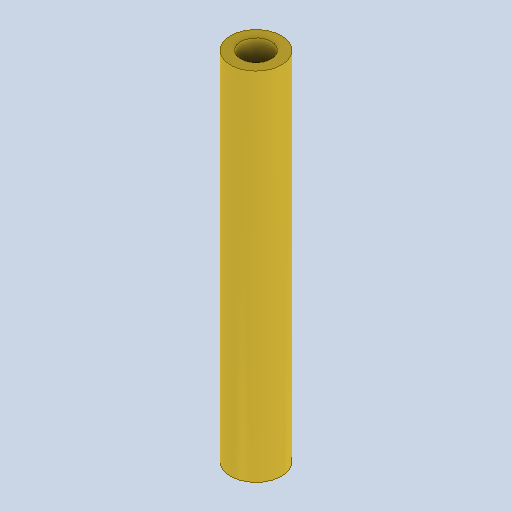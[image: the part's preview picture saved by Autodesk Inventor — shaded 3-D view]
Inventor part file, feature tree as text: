
AUTODESK INVENTOR PART (.ipt)
format: ipt  version: 2023 (Build 270158000, 158)  size: 231,424 bytes
history: native  units: in
note: dims shown in document units (in); Inventor stores cm internally (conversion verified against a paired STEP export)
features: extrude x1, sketch x1
ambient origin geometry x8: Origin, YZ Plane, XZ Plane, XY Plane, X Axis, Y Axis, Z Axis, Center Point
bodies: Solid1 (feature_tree)
feature tree (2):
  extrude  "Extrusion1"  Depth=1.378in
  sketch  "Sketch1"  dims[d0=0.1969in d1=0.1181in d2=1.378in d3=0.0in]
